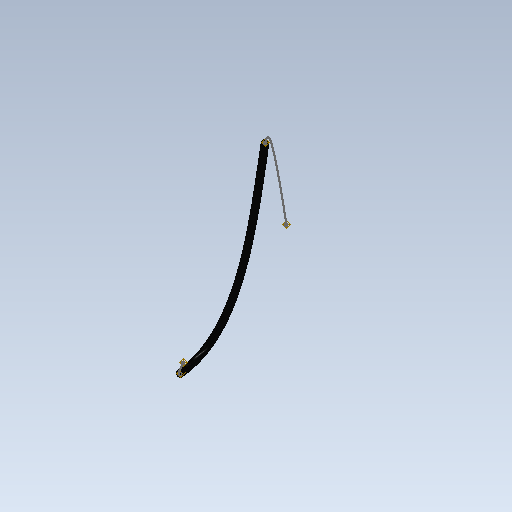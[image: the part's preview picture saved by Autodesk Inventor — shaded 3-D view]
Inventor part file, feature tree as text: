
AUTODESK INVENTOR PART (.ipt)
format: ipt  version: 2020 (Build 240168000, 168)  size: 107,520 bytes
history: native  units: mm (DEFAULTED — no unit token found)
features: other x16, plane x1, sketch x1
bodies: Body1 (feature_tree)
feature tree (18):
  other  "Origen"
  other  "Punto de trabajo1"
  other  "Punto de trabajo2"
  other  "Conductor1"
  other  "Punto de trabajo3"
  other  "Punto de trabajo4"
  other  "Segmento1"
  other  "Punto de trabajo5"
  plane  "Plano de trabajo1"
  other  "Plano YZ"
  other  "Plano XZ"
  other  "Plano XY"
  other  "Eje X"
  other  "Eje Y"
  other  "Eje Z"
  sketch  "Boceto1"  dims[d0=0.0mm d1=0.0mm]
  other  "Sup1"
  other  "SuperficieBarrido1"
